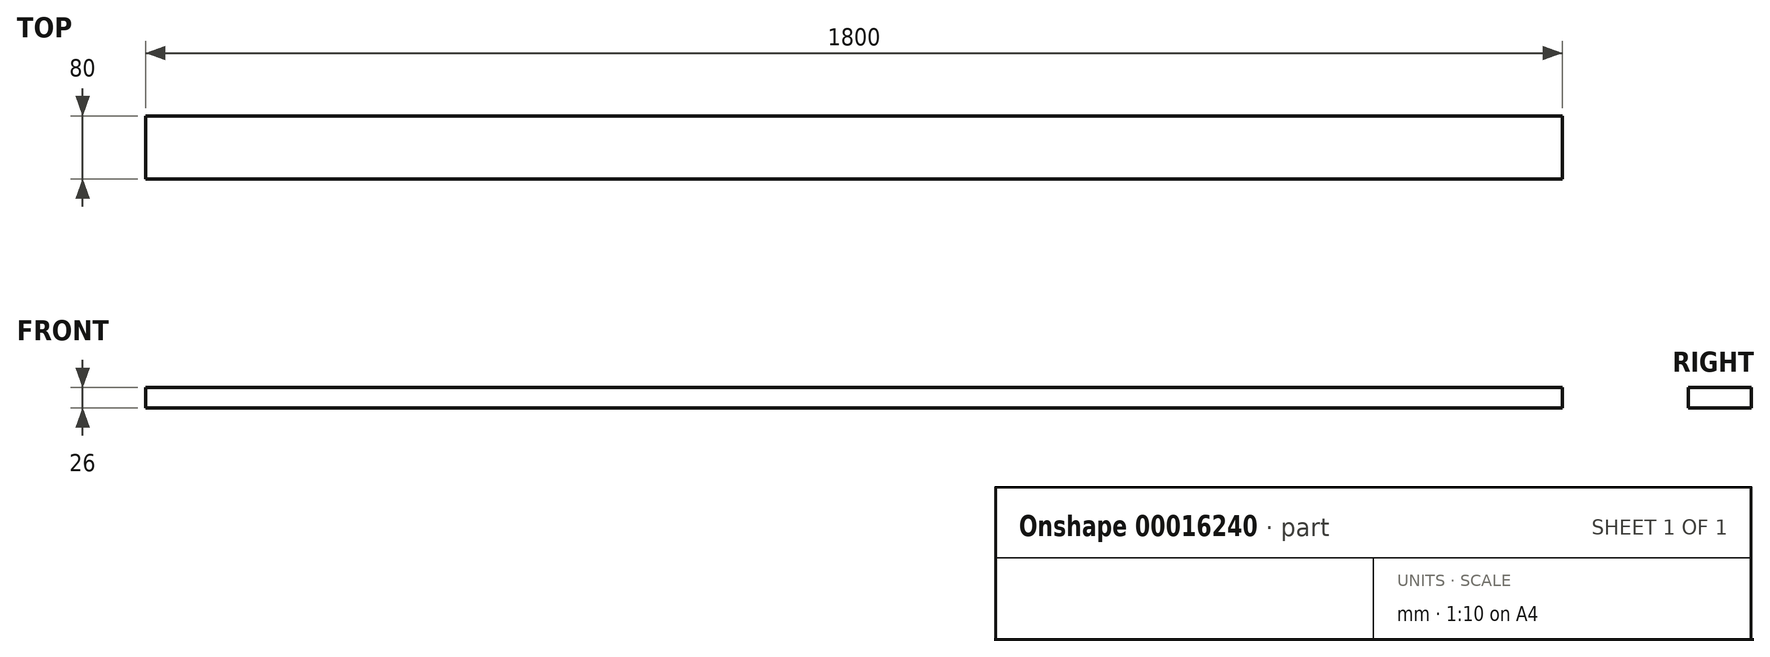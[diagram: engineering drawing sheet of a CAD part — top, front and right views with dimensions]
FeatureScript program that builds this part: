
annotation { "Feature Type Name" : "Feature", "Feature Type Description" : "" }
export const myFeature = defineFeature(function(context is Context, id is Id, definition is map)
    precondition{}
    {
        {
            var Q0;
            Q0=qCreatedBy(makeId("Top.planeOp"),FACE);
            var sketch = newSketch(context, id + "F0", { "sketchPlane" : qUnion([Q0])});
            skLineSegment(sketch, "E0.bottom", {"start": v(-127.08, 44.96) * mm, "end": v(1672.92, 44.96) * mm});
            skLineSegment(sketch, "E0.top", {"start": v(-127.08, -35.04) * mm, "end": v(1672.92, -35.04) * mm});
            skLineSegment(sketch, "E0.left", {"start": v(-127.08, 44.96) * mm, "end": v(-127.08, -35.04) * mm});
            skLineSegment(sketch, "E0.right", {"start": v(1672.92, 44.96) * mm, "end": v(1672.92, -35.04) * mm});
            skSolve(sketch);
        }
        {
            var Q0;
            Q0=makeQuery(id+"F0.imprint","IMPRINT",FACE,{"disambiguationData":[TD([[makeQuery(id+"F0.imprint","IMPRINT",EDGE,{"derivedFrom":sQuery(id+"F0.wireOp",EDGE,"E0.bottom")}),-1.0]])]});
            extrude(context, id + "F1", {"entities" : qUnion([Q0]), "depth" : 26 * mm});
        }
    });
